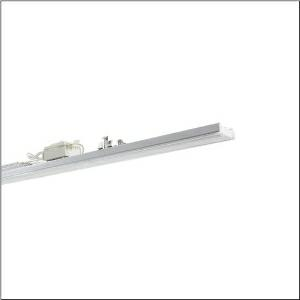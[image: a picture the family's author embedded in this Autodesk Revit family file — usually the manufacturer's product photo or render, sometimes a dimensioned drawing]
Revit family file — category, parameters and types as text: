
# Revit family: licross_r__11_recessed_mo_51tl14cn485g_fd8e
name_source: partatom
category: Lighting Fixtures
units: mm (PartAtom-declared; Revit-internal decimal feet)

## family parameters
Cut with Voids When Loaded = No
Host = Face
Light Source = No
Part Type = Normal
Room Calculation Point = No
Round Connector Dimension = Use Diameter
Shared = No

## types (1)
- --- (1 x LED, 8570 lm, 49.3 W, 4000K)
    Apparent Load = 49 VA
    CIE Flux Codes = 56 84 97 100 100
    Color Rendering = 80
    Color Temperature = 4000K
    Default Elevation = 1800 mm
    Description = Licross® 11 Recessed MO, luminaire insert, of sheet steel, coil coated, white, length: 1.500mm, width: 66mm, height: 67mm, LED rated luminous flux: 8.570lm, light colour: 840, control gear: ON/OFF Multilumen, CLOi, with plug, 3-pole, with phase selection, mains connection: 220..240V, AC, 50/60Hz, start of lifetime: 49W, end of service life: 55W, halogen-free wiring, primary light control with lens, of plastic, primary optical cover: cover, of PMMA, light emission: direct distribution, primary light characteristic: asymmetric, protection rating (complete): IP40, insulation class (complete): insulation class I (protective earthing), certification: CE, ENEC, VDE, UKCA, protection symbol: D if used in an environment without relevant dust loads with corresponding accessories, impact resistance: IK06, permissible ambient temperature for indoor applications: -35..+40°C, corresponds to IFS (International Featured Standards) requirements for safety and quality in the food industry, reducing of maximum allowable ambient temperature of 5°C with ceiling mounting, LABS conformity tested according to VDMA 24364:2018-05, packaging unit: 1 piece
    Height = 58 mm
    Lamp = 1 x LED
    Lamp Light Flux = 8570 lm
    Lamp Power = 49.3 W
    Lamp count = 1
    Length = 1500 mm
    Luminous efficacy = 174 lm/W
    Manufacturer = Siteco
    ModVariant = No
    Model = 51TL14CN485G
    Mounting Place = Ceiling
    Mounting Type = Pendant
    Number of Poles = 1
    OnlyDefault = Yes
    Power Factor = 1
    Product Name = Licross® 11 Recessed MO
    Product group = luminaire insert
    ProductGroupID = 902
    Protection Class = Protection class I
    Protection Degree = IP 40
    RLX_Detail_Level = 1
    RLX_Emergency_Light_Flux = 0 lm
    RLX_Emergency_Type = 0
    RLX_Emergency_Type_DB = No
    RlxData = <blob elided: 22773 chars, md5=bc75f38d>
    Socket = socket
    Standby Power = 0 W
    System Light Flux = 8570 lm
    System Power = 49 W
    Type Comments = factory setting: luminous flux: 100 % | (A | C | E) | 113 mA
    Type Image = l_1296930.jpg
    URL = http://relux.com
    VarID = @adj_085222
    Voltage = 0 V
    Weight = 0.00 kg
    Width = 66 mm

## geometry (parser evidence)
native form markers: Blend x4, Sweep x12
no freeform markers — native parametric forms only
